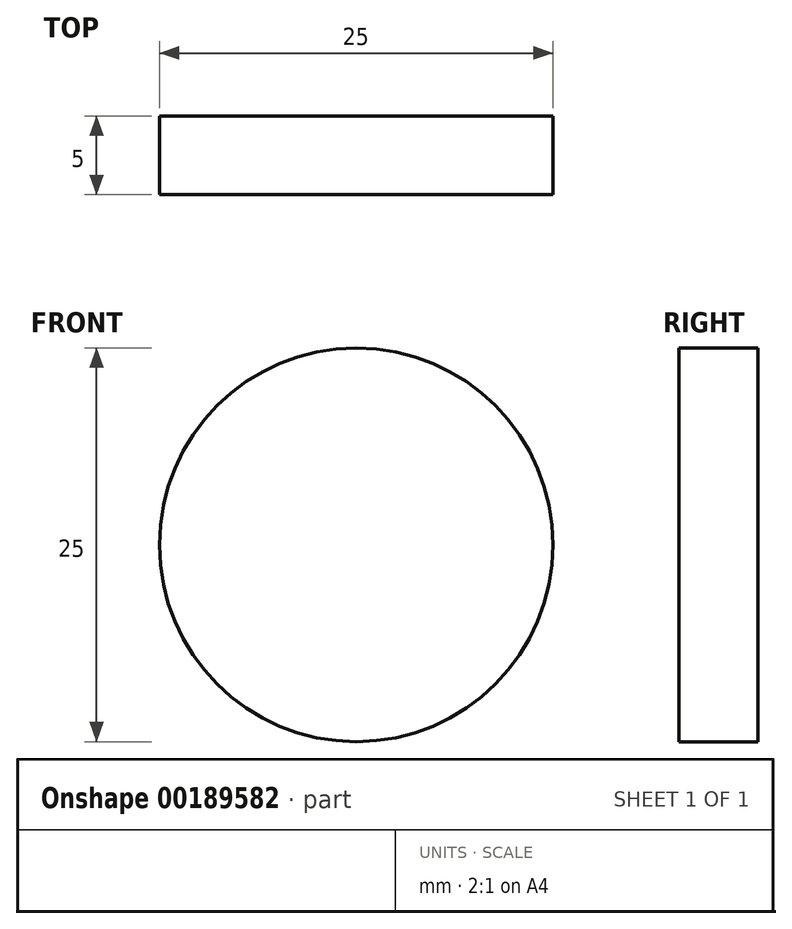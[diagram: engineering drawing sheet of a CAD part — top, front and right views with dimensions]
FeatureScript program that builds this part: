
annotation { "Feature Type Name" : "Feature", "Feature Type Description" : "" }
export const myFeature = defineFeature(function(context is Context, id is Id, definition is map)
    precondition{}
    {
        {
            var Q0;
            Q0=qCreatedBy(makeId("Front.planeOp"),FACE);
            var sketch = newSketch(context, id + "F0", { "sketchPlane" : qUnion([Q0])});
            skCircle(sketch, "E0", {"center": v(0, 0) * mm, "radius": 12.5 * mm});
            skSolve(sketch);
        }
        {
            var Q0;
            Q0=makeQuery(id+"F0.imprint","IMPRINT",FACE,{"disambiguationData":[TD([[makeQuery(id+"F0.imprint","IMPRINT",EDGE,{"derivedFrom":sQuery(id+"F0.wireOp",EDGE,"E0")}),1.0]])]});
            extrude(context, id + "F1", {"entities" : qUnion([Q0]), "depth" : 5 * mm});
        }
    });
